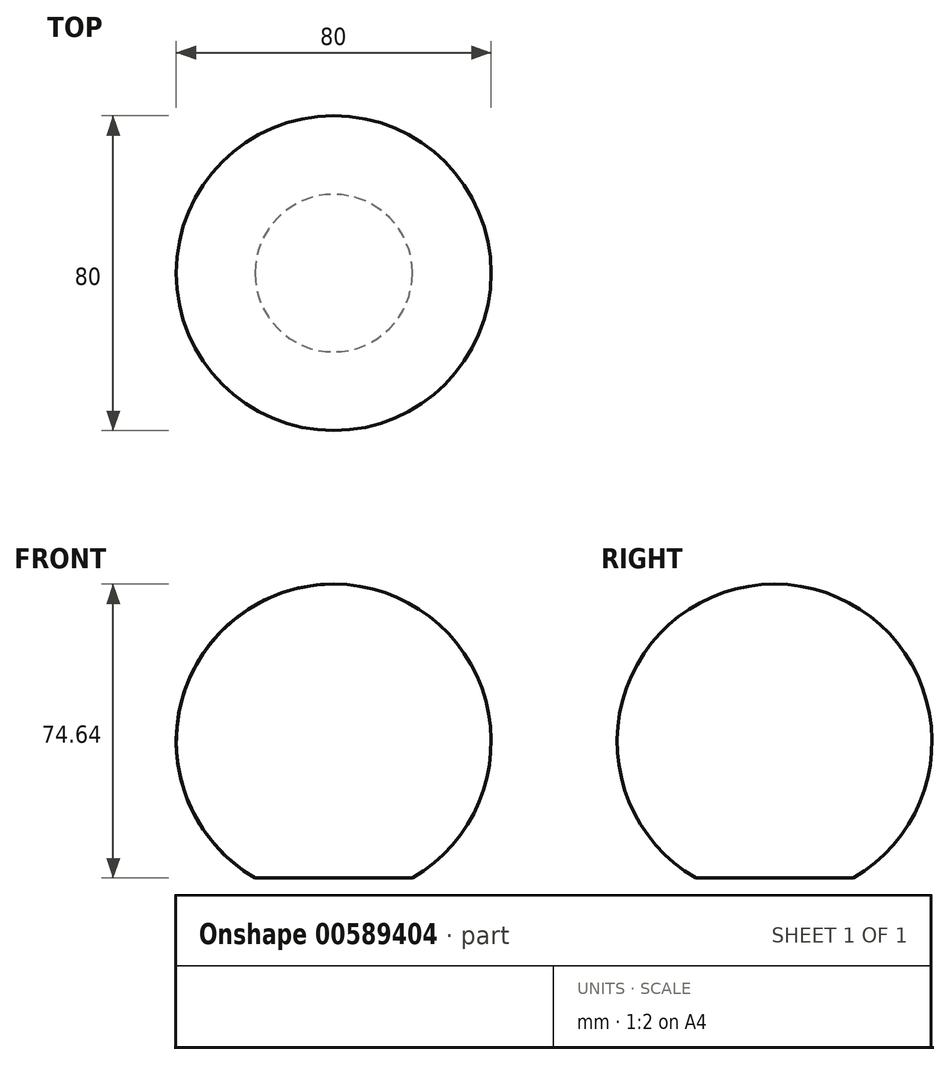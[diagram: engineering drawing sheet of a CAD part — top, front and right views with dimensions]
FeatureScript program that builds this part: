
annotation { "Feature Type Name" : "Feature", "Feature Type Description" : "" }
export const myFeature = defineFeature(function(context is Context, id is Id, definition is map)
    precondition{}
    {
        {
            var Q0;
            Q0=qCreatedBy(makeId("Front.planeOp"),FACE);
            var sketch = newSketch(context, id + "F0", { "sketchPlane" : qUnion([Q0])});
            skArc(sketch, "E0", {"start": v(0, -40) * mm, "mid": v(-10.35, -38.64) * mm, "end": v(-20, -34.64) * mm, "construction": true});
            skLineSegment(sketch, "E1", {"start": v(-20, -34.64) * mm, "end": v(0, -34.64) * mm});
            skArc(sketch, "E2", {"start": v(-20, -34.64) * mm, "mid": v(-38.64, 10.35) * mm, "end": v(0, 40) * mm});
            skLineSegment(sketch, "E3", {"start": v(0, 67.17) * mm, "end": v(0, -62.6) * mm, "construction": true});
            skLineSegment(sketch, "E4", {"start": v(0, 40) * mm, "end": v(0, -34.64) * mm});
            skSolve(sketch);
        }
        {
            var Q0;
            Q0=makeQuery(id+"F0.imprint","IMPRINT",FACE,{"disambiguationData":[TD([[makeQuery(id+"F0.imprint","IMPRINT",EDGE,{"derivedFrom":sQuery(id+"F0.wireOp",EDGE,"E1")}),1.0]])]});
            var Q1;
            Q1=sQuery(id+"F0.wireOp",EDGE,"E2");
            var Q2;
            Q2=sQuery(id+"F0.wireOp",EDGE,"E1");
            var Q3;
            Q3=sQuery(id+"F0.wireOp",EDGE,"E3");
            revolve(context, id + "F1", {"entities" : qUnion([Q0]), "surfaceEntities" : qUnion([Q1, Q2]), "axis" : qUnion([Q3]), "revolveType" : RevolveType.FULL});
        }
    });
